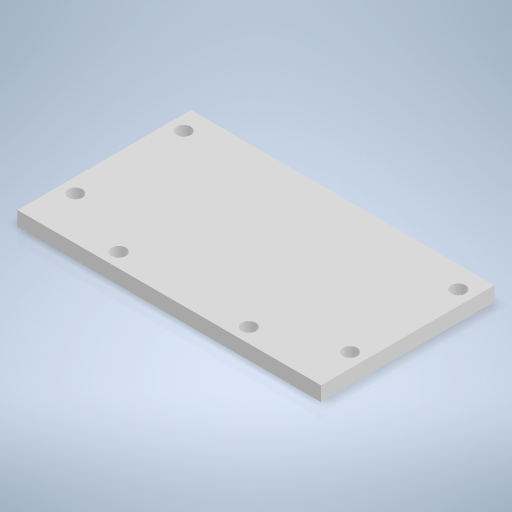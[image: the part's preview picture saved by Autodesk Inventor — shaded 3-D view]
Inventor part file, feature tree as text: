
AUTODESK INVENTOR PART (.ipt)
format: ipt  version: 2024 (Build 280153000, 153)  size: 231,936 bytes
history: native  units: mm
features: sketch x3, hole x2, extrude x1
ambient origin geometry x8: Origin, YZ Plane, XZ Plane, XY Plane, X Axis, Y Axis, Z Axis, Center Point
bodies: Volumenkörper1 (feature_tree)
feature tree (6):
  extrude  "Extrusion1"  Depth=84.0mm
  hole  "Bohrung1"  [1 undecoded]
  hole  "Bohrung2"  [1 undecoded]
  sketch  "Skizze1"  dims[d0=48.0mm d1=84.0mm]
  sketch  "Skizze2"  dims[d2=4.0mm d3=0.0mm d4=4.0mm]
  sketch  "Skizze3"  dims[d5=30.0mm d6=12.0mm d7=4.0mm d8=4.0mm d9=6.0mm d10=6.0mm d11=2.0mm d12=90.0deg d13=8.0mm d14=0.0mm d15=4.0mm d16=24.0mm d17=36.0mm d18=4.0mm d19=6.0mm d20=4.0mm d21=2.0mm d22=90.0deg d23=8.0mm d24=0.0mm]
note: 2 required parameter values undecoded (feature->parameter linkage not recoverable at this tier; creation-order binding heuristic only, values carry confidence <= 0.55)
